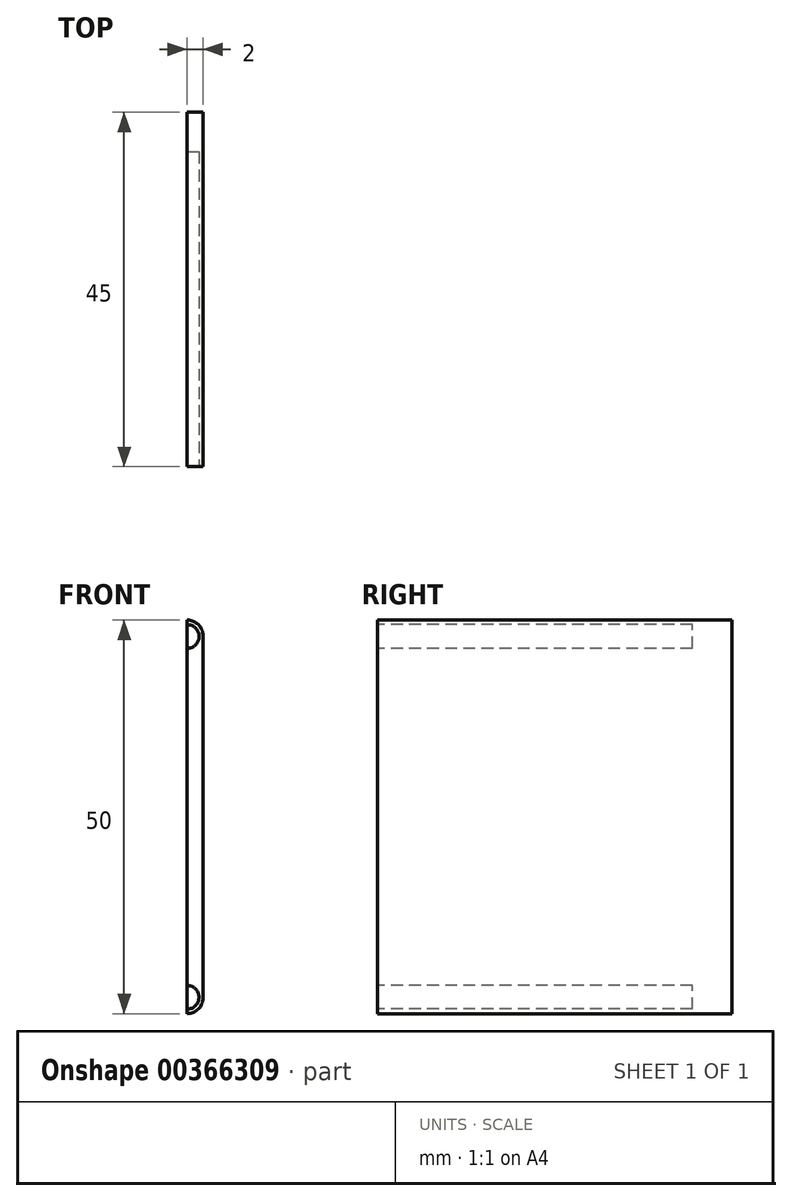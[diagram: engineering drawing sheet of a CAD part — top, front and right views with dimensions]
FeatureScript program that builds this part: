
annotation { "Feature Type Name" : "Feature", "Feature Type Description" : "" }
export const myFeature = defineFeature(function(context is Context, id is Id, definition is map)
    precondition{}
    {
        {
            var Q0;
            Q0=qCreatedBy(makeId("Front.planeOp"),FACE);
            var sketch = newSketch(context, id + "F0", { "sketchPlane" : qUnion([Q0])});
            skLineSegment(sketch, "E0.bottom", {"start": v(0, 0) * mm, "end": v(-2, 0) * mm});
            skLineSegment(sketch, "E0.top", {"start": v(0, 50) * mm, "end": v(-2, 50) * mm});
            skLineSegment(sketch, "E0.left", {"start": v(0, 0) * mm, "end": v(0, 50) * mm});
            skLineSegment(sketch, "E0.right", {"start": v(-2, 0) * mm, "end": v(-2, 50) * mm});
            skSolve(sketch);
        }
        {
            var Q0;
            Q0=makeQuery(id+"F0.imprint","IMPRINT",FACE,{"disambiguationData":[TD([[makeQuery(id+"F0.imprint","IMPRINT",EDGE,{"derivedFrom":sQuery(id+"F0.wireOp",EDGE,"E0.bottom")}),-1.0]])]});
            extrude(context, id + "F1", {"entities" : qUnion([Q0]), "depth" : 45 * mm});
        }
        {
            var Q0;
            Q0=makeQuery(id+"F1.opExtrude","SWEPT_EDGE",EDGE,{"disambiguationData":[OSD([sQuery(id+"F0.wireOp",EDGE,"E0.bottom"),sQuery(id+"F0.wireOp",EDGE,"E0.left")])]});
            var Q1;
            Q1=makeQuery(id+"F1.opExtrude","SWEPT_EDGE",EDGE,{"disambiguationData":[OSD([sQuery(id+"F0.wireOp",EDGE,"E0.top"),sQuery(id+"F0.wireOp",EDGE,"E0.left")])]});
            fillet(context, id + "F2", {"entities" : qUnion([Q0, Q1]), "radius" : 2 * mm, "tangentPropagation" : true, "allowEdgeOverflow" : false});
        }
        {
            var Q0;
            Q0=makeQuery(id+"F1.opExtrude","CAP_FACE",FACE,{"disambiguationData":[OSD([sQuery(id+"F0.wireOp",EDGE,"E0.bottom"),sQuery(id+"F0.wireOp",EDGE,"E0.top"),sQuery(id+"F0.wireOp",EDGE,"E0.left"),sQuery(id+"F0.wireOp",EDGE,"E0.right")])],"isStart":false});
            var sketch = newSketch(context, id + "F3", { "sketchPlane" : qUnion([Q0])});
            skArc(sketch, "E1", {"start": v(-2, 46.41) * mm, "mid": v(-0.5, 47.91) * mm, "end": v(-2, 49.41) * mm});
            skPoint(sketch, "E1.endSnap0", {"position": v(-0.59, 49.41) * mm});
            skArc(sketch, "E2", {"start": v(-2, 0.59) * mm, "mid": v(-0.5, 2.09) * mm, "end": v(-2, 3.59) * mm});
            skPoint(sketch, "E2.startSnap0", {"position": v(-0.59, 0.59) * mm});
            skSolve(sketch);
        }
        {
            var Q0;
            {var subQ0=sQuery(id+"F3.wireOp",EDGE,"E1");Q0=makeQuery(id+"F3.imprint","IMPRINT",FACE,{"disambiguationData":[TD([[makeQuery(id+"F3.imprint","IMPRINT",EDGE,{"derivedFrom":subQ0}),1.0]])]});}
            var Q1;
            {var subQ0=sQuery(id+"F3.wireOp",EDGE,"E2");Q1=makeQuery(id+"F3.imprint","IMPRINT",FACE,{"disambiguationData":[TD([[makeQuery(id+"F3.imprint","IMPRINT",EDGE,{"derivedFrom":subQ0}),1.0]])]});}
            extrude(context, id + "F4", {"entities" : qUnion([Q0, Q1]), "operationType" : NewBodyOperationType.REMOVE, "oppositeDirection" : true, "depth" : 40 * mm});
        }
    });
